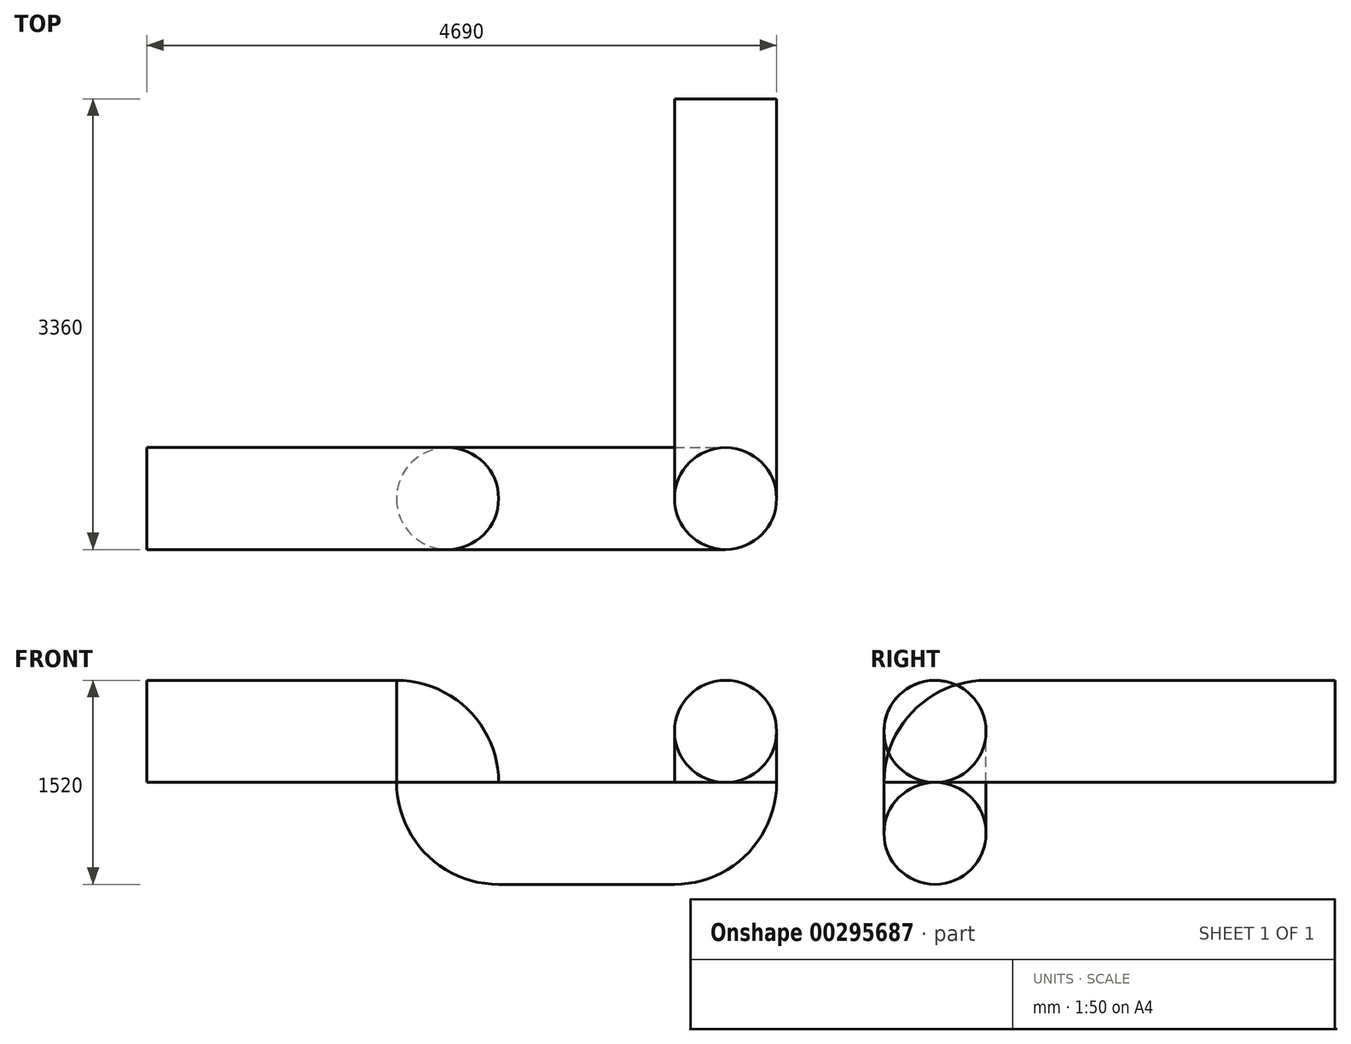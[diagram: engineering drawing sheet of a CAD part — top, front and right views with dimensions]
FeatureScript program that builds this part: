
annotation { "Feature Type Name" : "Feature", "Feature Type Description" : "" }
export const myFeature = defineFeature(function(context is Context, id is Id, definition is map)
    precondition{}
    {
        {
            var Q0;
            Q0=qCreatedBy(makeId("Front.planeOp"),FACE);
            var sketch = newSketch(context, id + "F0", { "sketchPlane" : qUnion([Q0])});
            skCircle(sketch, "E0", {"center": v(0, 0) * mm, "radius": 380 * mm});
            skSolve(sketch);
        }
        {
            var Q0;
            Q0=qCreatedBy(makeId("Right.planeOp"),FACE);
            var sketch = newSketch(context, id + "F1", { "sketchPlane" : qUnion([Q0])});
            skLineSegment(sketch, "E1", {"start": v(0, 0) * mm, "end": v(-2600, 0) * mm});
            skArc(sketch, "E2", {"start": v(-2600, 0) * mm, "mid": v(-2868.7, -111.3) * mm, "end": v(-2980, -380) * mm});
            skLineSegment(sketch, "E3", {"start": v(-1620, -380) * mm, "end": v(-3117.27, -380) * mm, "construction": true});
            skSolve(sketch);
        }
        {
            var Q0;
            Q0=qCreatedBy(makeId("Front.planeOp"),FACE);
            var Q1;
            Q1=sQuery(id+"F1.wireOp",VERTEX,"E2.end");
            cPlane(context, id + "F2", {"entities" : qUnion([Q0, Q1]), "cplaneType" : CPlaneType.PLANE_POINT, "offset" : 25 * mm, "width" : 150 * mm, "height" : 150 * mm});
        }
        {
            var Q0;
            Q0=qCreatedBy(id+"F2.planeOp",FACE);
            var sketch = newSketch(context, id + "F3", { "sketchPlane" : qUnion([Q0])});
            skArc(sketch, "E4", {"start": v(0, -380) * mm, "mid": v(-111.3, -648.7) * mm, "end": v(-380, -760) * mm});
            skLineSegment(sketch, "E5", {"start": v(0, -380) * mm, "end": v(-2070, -380) * mm, "construction": true});
            skLineSegment(sketch, "E6", {"start": v(-380, -380) * mm, "end": v(-380, -1008.4) * mm, "construction": true});
            skLineSegment(sketch, "E7", {"start": v(-380, -760) * mm, "end": v(-1690, -760) * mm});
            skArc(sketch, "E8", {"start": v(-1690, -760) * mm, "mid": v(-1958.7, -648.7) * mm, "end": v(-2070, -380) * mm});
            skArc(sketch, "E9", {"start": v(-2070, -380) * mm, "mid": v(-2181.3, -111.3) * mm, "end": v(-2450, 0) * mm});
            skLineSegment(sketch, "E10", {"start": v(-2450, 0) * mm, "end": v(-4310, 0) * mm});
            skLineSegment(sketch, "E11", {"start": v(-2450, -545.64) * mm, "end": v(-2450, 477.38) * mm, "construction": true});
            skSolve(sketch);
        }
        {
            var Q0;
            Q0=makeQuery(id+"F0.imprint","IMPRINT",FACE,{"disambiguationData":[TD([[makeQuery(id+"F0.imprint","IMPRINT",EDGE,{"derivedFrom":sQuery(id+"F0.wireOp",EDGE,"E0")}),1.0]])]});
            var Q1;
            Q1=sQuery(id+"F1.wireOp",EDGE,"E1");
            var Q2;
            Q2=sQuery(id+"F1.wireOp",EDGE,"E2");
            var Q3;
            Q3=sQuery(id+"F3.wireOp",EDGE,"E4");
            var Q4;
            Q4=sQuery(id+"F3.wireOp",EDGE,"E7");
            var Q5;
            Q5=sQuery(id+"F3.wireOp",EDGE,"E8");
            var Q6;
            Q6=sQuery(id+"F3.wireOp",EDGE,"E9");
            var Q7;
            Q7=sQuery(id+"F3.wireOp",EDGE,"E10");
            sweep(context, id + "F4", {"profiles" : qUnion([Q0]), "path" : qUnion([Q1, Q2, Q3, Q4, Q5, Q6, Q7])});
        }
    });
